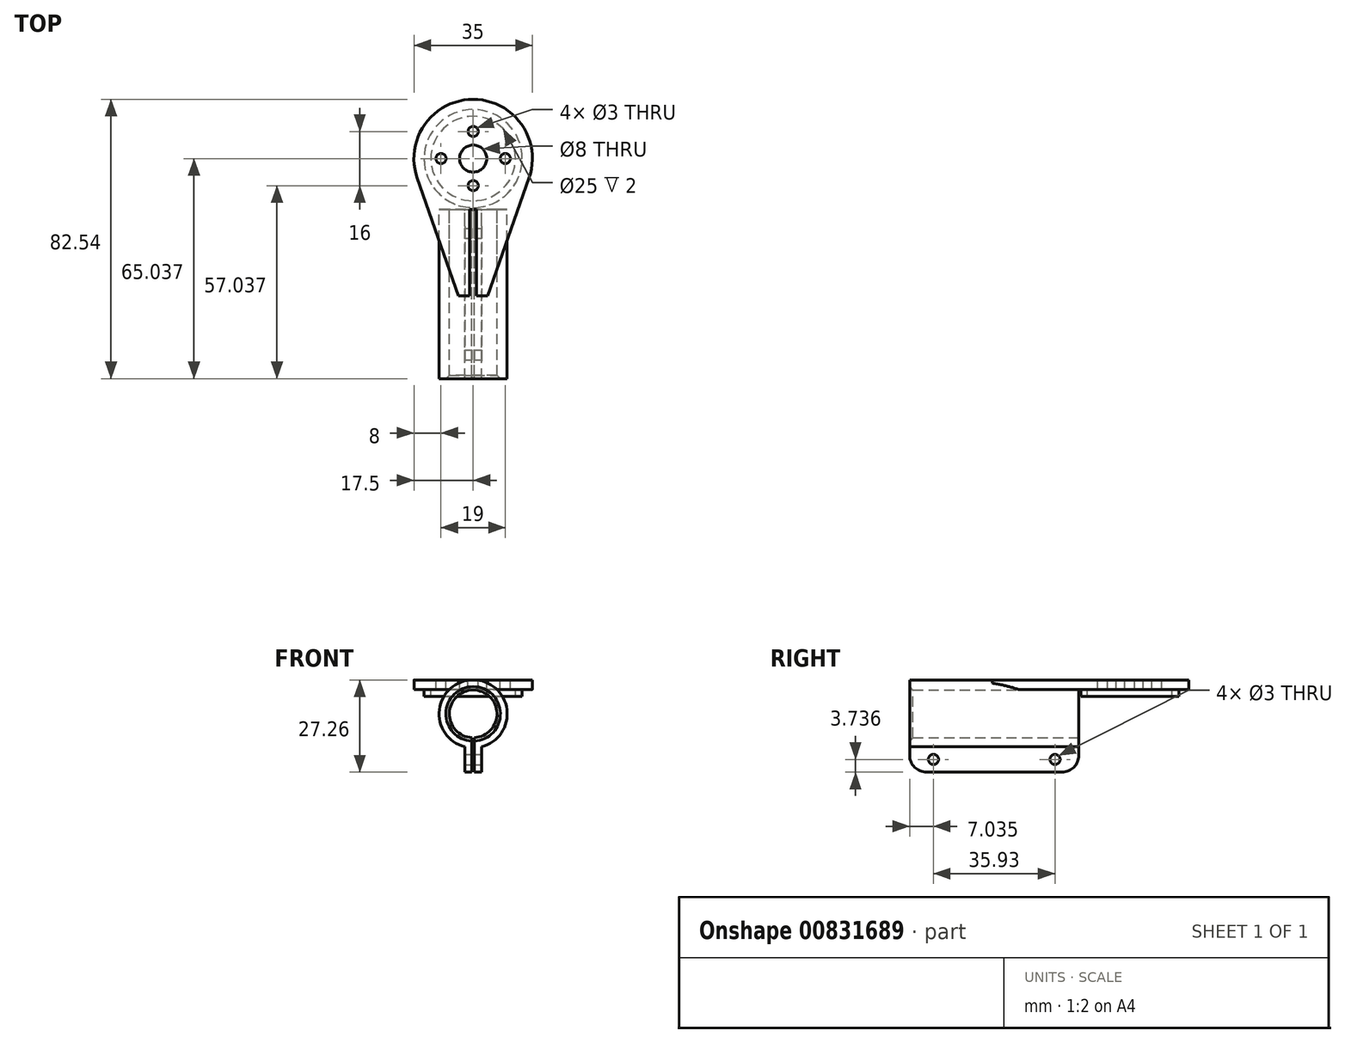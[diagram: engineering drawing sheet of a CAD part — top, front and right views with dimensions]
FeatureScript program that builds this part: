
annotation { "Feature Type Name" : "Feature", "Feature Type Description" : "" }
export const myFeature = defineFeature(function(context is Context, id is Id, definition is map)
    precondition{}
    {
        {
            var Q0;
            Q0=qCreatedBy(makeId("Front.planeOp"),FACE);
            var sketch = newSketch(context, id + "F0", { "sketchPlane" : qUnion([Q0])});
            skCircle(sketch, "E0", {"center": v(0, 0) * mm, "radius": 7.05 * mm});
            skCircle(sketch, "E1.0", {"center": v(0, 0) * mm, "radius": 10.05 * mm});
            skSolve(sketch);
        }
        {
            var Q0;
            Q0 = qSketchRegion(id + "F0", true);
            extrude(context, id + "F1", {"entities" : qUnion([Q0]), "depth" : 50 * mm, "offsetDistance" : 25 * mm});
        }
        {
            var Q0;
            Q0=qCreatedBy(makeId("Top.planeOp"),FACE);
            cPlane(context, id + "F2", {"entities" : qUnion([Q0]), "cplaneType" : CPlaneType.OFFSET, "offset" : 10 * mm, "width" : 150 * mm, "height" : 150 * mm});
        }
        {
            var Q0;
            Q0=qCreatedBy(id+"F2.planeOp",FACE);
            var sketch = newSketch(context, id + "F3", { "sketchPlane" : qUnion([Q0])});
            skCircle(sketch, "E2", {"center": v(0, 15.04) * mm, "radius": 17.5 * mm});
            skSolve(sketch);
        }
        {
            var Q0;
            Q0 = qSketchRegion(id + "F3", true);
            extrude(context, id + "F4", {"entities" : qUnion([Q0]), "operationType" : NewBodyOperationType.ADD, "oppositeDirection" : true, "depth" : 2.8 * mm, "offsetDistance" : 25 * mm});
        }
        {
            var Q0;
            Q0=makeQuery(id+"F1.opExtrude","CAP_FACE",FACE,{"disambiguationData":[OSD([sQuery(id+"F0.wireOp",EDGE,"E0"),sQuery(id+"F0.wireOp",EDGE,"E1.0")])],"isStart":false});
            var sketch = newSketch(context, id + "F5", { "sketchPlane" : qUnion([Q0])});
            skLineSegment(sketch, "E3.bottom", {"start": v(2.5, -17.21) * mm, "end": v(-2.5, -17.21) * mm});
            skLineSegment(sketch, "E3.top", {"start": v(2.5, -7.21) * mm, "end": v(-2.5, -7.21) * mm});
            skLineSegment(sketch, "E3.left", {"start": v(2.5, -17.21) * mm, "end": v(2.5, -7.21) * mm});
            skLineSegment(sketch, "E3.right", {"start": v(-2.5, -17.21) * mm, "end": v(-2.5, -7.21) * mm});
            skLineSegment(sketch, "E4", {"start": v(0, -16.9) * mm, "end": v(0, 0) * mm, "construction": true});
            skSolve(sketch);
        }
        {
            var Q0;
            Q0 = qSketchRegion(id + "F5", true);
            var Q1;
            {var subQ0=sQuery(id+"F0.wireOp",EDGE,"E0");var subQ1=sQuery(id+"F0.wireOp",EDGE,"E1.0");Q1=makeQuery(id+"F4.boolean.opBoolean","SPLIT",FACE,{"disambiguationData":[TD([makeQuery(id+"F1.opExtrude","SWEPT_FACE",FACE,{"disambiguationData":[OSD([subQ0])]})])],"derivedFrom":makeQuery(id+"F1.opExtrude","CAP_FACE",FACE,{"disambiguationData":[OSD([subQ0,subQ1])],"isStart":true})});}
            extrude(context, id + "F6", {"entities" : qUnion([Q0]), "operationType" : NewBodyOperationType.ADD, "endBound" : BoundingType.UP_TO_SURFACE, "oppositeDirection" : true, "depth" : 25 * mm, "endBoundEntityFace" : qUnion([Q1]), "offsetDistance" : 25 * mm});
        }
        {
            var Q0;
            Q0=makeQuery(id+"F6.boolean.opBoolean","MERGE",FACE,{"derivedFrom":[makeQuery(id+"F1.opExtrude","CAP_FACE",FACE,{"disambiguationData":[OSD([sQuery(id+"F0.wireOp",EDGE,"E0"),sQuery(id+"F0.wireOp",EDGE,"E1.0")])],"isStart":false}),makeQuery(id+"F6.opExtrude","CAP_FACE",FACE,{"disambiguationData":[OSD([sQuery(id+"F5.wireOp",EDGE,"E3.bottom"),sQuery(id+"F5.wireOp",EDGE,"E3.top"),sQuery(id+"F5.wireOp",EDGE,"E3.left"),sQuery(id+"F5.wireOp",EDGE,"E3.right")])],"isStart":true})]});
            var sketch = newSketch(context, id + "F7", { "sketchPlane" : qUnion([Q0])});
            skLineSegment(sketch, "E5.bottom", {"start": v(0.4, -18.92) * mm, "end": v(-0.4, -18.92) * mm});
            skLineSegment(sketch, "E5.top", {"start": v(0.4, -6.29) * mm, "end": v(-0.4, -6.29) * mm});
            skLineSegment(sketch, "E5.left", {"start": v(0.4, -18.92) * mm, "end": v(0.4, -6.29) * mm});
            skLineSegment(sketch, "E5.right", {"start": v(-0.4, -18.92) * mm, "end": v(-0.4, -6.29) * mm});
            skSolve(sketch);
        }
        {
            var Q0;
            Q0 = qSketchRegion(id + "F7", true);
            extrude(context, id + "F8", {"entities" : qUnion([Q0]), "operationType" : NewBodyOperationType.REMOVE, "endBound" : BoundingType.THROUGH_ALL, "oppositeDirection" : true, "depth" : 25 * mm, "offsetDistance" : 25 * mm});
        }
        {
            var Q0;
            Q0=makeQuery(id+"F4.opExtrude","CAP_FACE",FACE,{"disambiguationData":[OSD([sQuery(id+"F3.wireOp",EDGE,"E2")])],"isStart":true});
            var sketch = newSketch(context, id + "F9", { "sketchPlane" : qUnion([Q0])});
            skLineSegment(sketch, "E6", {"start": v(16.51, 9.24) * mm, "end": v(4.3, -25.53) * mm});
            skLineSegment(sketch, "E7", {"start": v(4.3, -25.53) * mm, "end": v(-4.32, -25.53) * mm});
            skLineSegment(sketch, "E8", {"start": v(-4.32, -25.53) * mm, "end": v(-16.51, 9.24) * mm});
            skLineSegment(sketch, "E9", {"start": v(16.51, 9.24) * mm, "end": v(-24.1, 9.24) * mm, "construction": true});
            skLineSegment(sketch, "E10", {"start": v(-16.51, 9.24) * mm, "end": v(16.51, 9.24) * mm});
            skSolve(sketch);
        }
        {
            var Q0;
            Q0 = qSketchRegion(id + "F9", true);
            extrude(context, id + "F10", {"entities" : qUnion([Q0]), "operationType" : NewBodyOperationType.ADD, "oppositeDirection" : true, "depth" : 2.8 * mm, "offsetDistance" : 25 * mm});
        }
        {
            var Q0;
            Q0=makeQuery(id+"F10.boolean.opBoolean","MERGE",FACE,{"derivedFrom":[makeQuery(id+"F4.opExtrude","CAP_FACE",FACE,{"disambiguationData":[OSD([sQuery(id+"F3.wireOp",EDGE,"E2")])],"isStart":true}),makeQuery(id+"F10.opExtrude","CAP_FACE",FACE,{"disambiguationData":[OSD([sQuery(id+"F9.wireOp",EDGE,"E6"),sQuery(id+"F9.wireOp",EDGE,"E7"),sQuery(id+"F9.wireOp",EDGE,"E8"),sQuery(id+"F9.wireOp",EDGE,"E10")])],"isStart":true})]});
            var sketch = newSketch(context, id + "F11", { "sketchPlane" : qUnion([Q0])});
            skCircle(sketch, "E11", {"center": v(0, 15.04) * mm, "radius": 9.5 * mm, "construction": true});
            skCircle(sketch, "E12", {"center": v(0, 15.04) * mm, "radius": 8 * mm, "construction": true});
            skLineSegment(sketch, "E13", {"start": v(0, 15.04) * mm, "end": v(-24.64, 15.04) * mm, "construction": true});
            skLineSegment(sketch, "E14", {"start": v(0, 15.04) * mm, "end": v(0, 35.82) * mm, "construction": true});
            skCircle(sketch, "E15", {"center": v(0, 23.04) * mm, "radius": 1.5 * mm});
            skCircle(sketch, "E16", {"center": v(-9.5, 15.04) * mm, "radius": 1.5 * mm});
            skCircle(sketch, "E17.MirrorC", {"center": v(0, 7.04) * mm, "radius": 1.5 * mm});
            skCircle(sketch, "E18.MirrorC", {"center": v(9.5, 15.04) * mm, "radius": 1.5 * mm});
            skCircle(sketch, "E19", {"center": v(0, 15.04) * mm, "radius": 4 * mm});
            skSolve(sketch);
        }
        {
            var Q0;
            Q0 = qSketchRegion(id + "F11", true);
            extrude(context, id + "F12", {"entities" : qUnion([Q0]), "operationType" : NewBodyOperationType.REMOVE, "oppositeDirection" : true, "depth" : 25 * mm, "offsetDistance" : 25 * mm});
        }
        {
            var Q0;
            Q0=makeQuery(id+"F10.boolean.opBoolean","MERGE",FACE,{"derivedFrom":[makeQuery(id+"F4.opExtrude","CAP_FACE",FACE,{"disambiguationData":[OSD([sQuery(id+"F3.wireOp",EDGE,"E2")])],"isStart":false}),makeQuery(id+"F10.opExtrude","CAP_FACE",FACE,{"disambiguationData":[OSD([sQuery(id+"F9.wireOp",EDGE,"E6"),sQuery(id+"F9.wireOp",EDGE,"E7"),sQuery(id+"F9.wireOp",EDGE,"E8"),sQuery(id+"F9.wireOp",EDGE,"E10")])],"isStart":false})]});
            var sketch = newSketch(context, id + "F13", { "sketchPlane" : qUnion([Q0])});
            skCircle(sketch, "E20", {"center": v(0, -15.04) * mm, "radius": 12.5 * mm});
            skCircle(sketch, "E21.0", {"center": v(0, -15.04) * mm, "radius": 14.5 * mm});
            skSolve(sketch);
        }
        {
            var Q0;
            Q0 = qSketchRegion(id + "F13", true);
            extrude(context, id + "F14", {"entities" : qUnion([Q0]), "operationType" : NewBodyOperationType.ADD, "depth" : 2 * mm, "offsetDistance" : 25 * mm});
        }
        {
            var Q0;
            Q0=makeQuery(id+"F6.opExtrude","SWEPT_FACE",FACE,{"disambiguationData":[OSD([sQuery(id+"F5.wireOp",EDGE,"E3.left")])]});
            var sketch = newSketch(context, id + "F15", { "sketchPlane" : qUnion([Q0])});
            skLineSegment(sketch, "E22", {"start": v(0, -13.47) * mm, "end": v(-50, -13.47) * mm, "construction": true});
            skLineSegment(sketch, "E23", {"start": v(-25, -17.21) * mm, "end": v(-25, -8.96) * mm, "construction": true});
            skPoint(sketch, "E23.endSnap0", {"position": v(-25, -9.73) * mm});
            skCircle(sketch, "E24", {"center": v(-7.03, -13.47) * mm, "radius": 1.5 * mm});
            skCircle(sketch, "E25.MirrorC", {"center": v(-42.97, -13.47) * mm, "radius": 1.5 * mm});
            skSolve(sketch);
        }
        {
            var Q0;
            Q0 = qSketchRegion(id + "F15", true);
            extrude(context, id + "F16", {"entities" : qUnion([Q0]), "operationType" : NewBodyOperationType.REMOVE, "endBound" : BoundingType.THROUGH_ALL, "oppositeDirection" : true, "depth" : 25 * mm, "offsetDistance" : 25 * mm});
        }
        {
            var Q0;
            {var subQ0=sQuery(id+"F5.wireOp",EDGE,"E3.left");var subQ1=sQuery(id+"F5.wireOp",EDGE,"E3.bottom");Q0=makeQuery(id+"F8.boolean.opBoolean","SPLIT",EDGE,{"disambiguationData":[TD([makeQuery(id+"F6.opExtrude","SWEPT_FACE",FACE,{"disambiguationData":[OSD([subQ0])]})])],"derivedFrom":makeQuery(id+"F6.opExtrude","CAP_EDGE",EDGE,{"disambiguationData":[OSD([subQ1])],"isStart":true})});}
            var Q1;
            {var subQ0=sQuery(id+"F5.wireOp",EDGE,"E3.right");var subQ1=sQuery(id+"F5.wireOp",EDGE,"E3.bottom");Q1=makeQuery(id+"F8.boolean.opBoolean","SPLIT",EDGE,{"disambiguationData":[TD([makeQuery(id+"F6.opExtrude","SWEPT_FACE",FACE,{"disambiguationData":[OSD([subQ0])]})])],"derivedFrom":makeQuery(id+"F6.opExtrude","CAP_EDGE",EDGE,{"disambiguationData":[OSD([subQ1])],"isStart":true})});}
            var Q2;
            {var subQ0=sQuery(id+"F5.wireOp",EDGE,"E3.right");var subQ1=sQuery(id+"F5.wireOp",EDGE,"E3.bottom");Q2=makeQuery(id+"F8.boolean.opBoolean","SPLIT",EDGE,{"disambiguationData":[TD([makeQuery(id+"F6.opExtrude","SWEPT_FACE",FACE,{"disambiguationData":[OSD([subQ0])]})])],"derivedFrom":makeQuery(id+"F6.opExtrude","CAP_EDGE",EDGE,{"disambiguationData":[OSD([subQ1])],"isStart":false})});}
            var Q3;
            {var subQ0=sQuery(id+"F5.wireOp",EDGE,"E3.left");var subQ1=sQuery(id+"F5.wireOp",EDGE,"E3.bottom");Q3=makeQuery(id+"F8.boolean.opBoolean","SPLIT",EDGE,{"disambiguationData":[TD([makeQuery(id+"F6.opExtrude","SWEPT_FACE",FACE,{"disambiguationData":[OSD([subQ0])]})])],"derivedFrom":makeQuery(id+"F6.opExtrude","CAP_EDGE",EDGE,{"disambiguationData":[OSD([subQ1])],"isStart":false})});}
            fillet(context, id + "F17", {"entities" : qUnion([Q0, Q1, Q2, Q3]), "radius" : 5 * mm, "tangentPropagation" : true, "allowEdgeOverflow" : false});
        }
        {
            var Q0;
            Q0=makeQuery(id+"F1.opExtrude","CAP_EDGE",EDGE,{"disambiguationData":[OSD([sQuery(id+"F0.wireOp",EDGE,"E0")])],"isStart":false});
            chamfer(context, id + "F18", {"entities" : qUnion([Q0]), "width" : 1 * mm, "tangentPropagation" : true});
        }
    });
